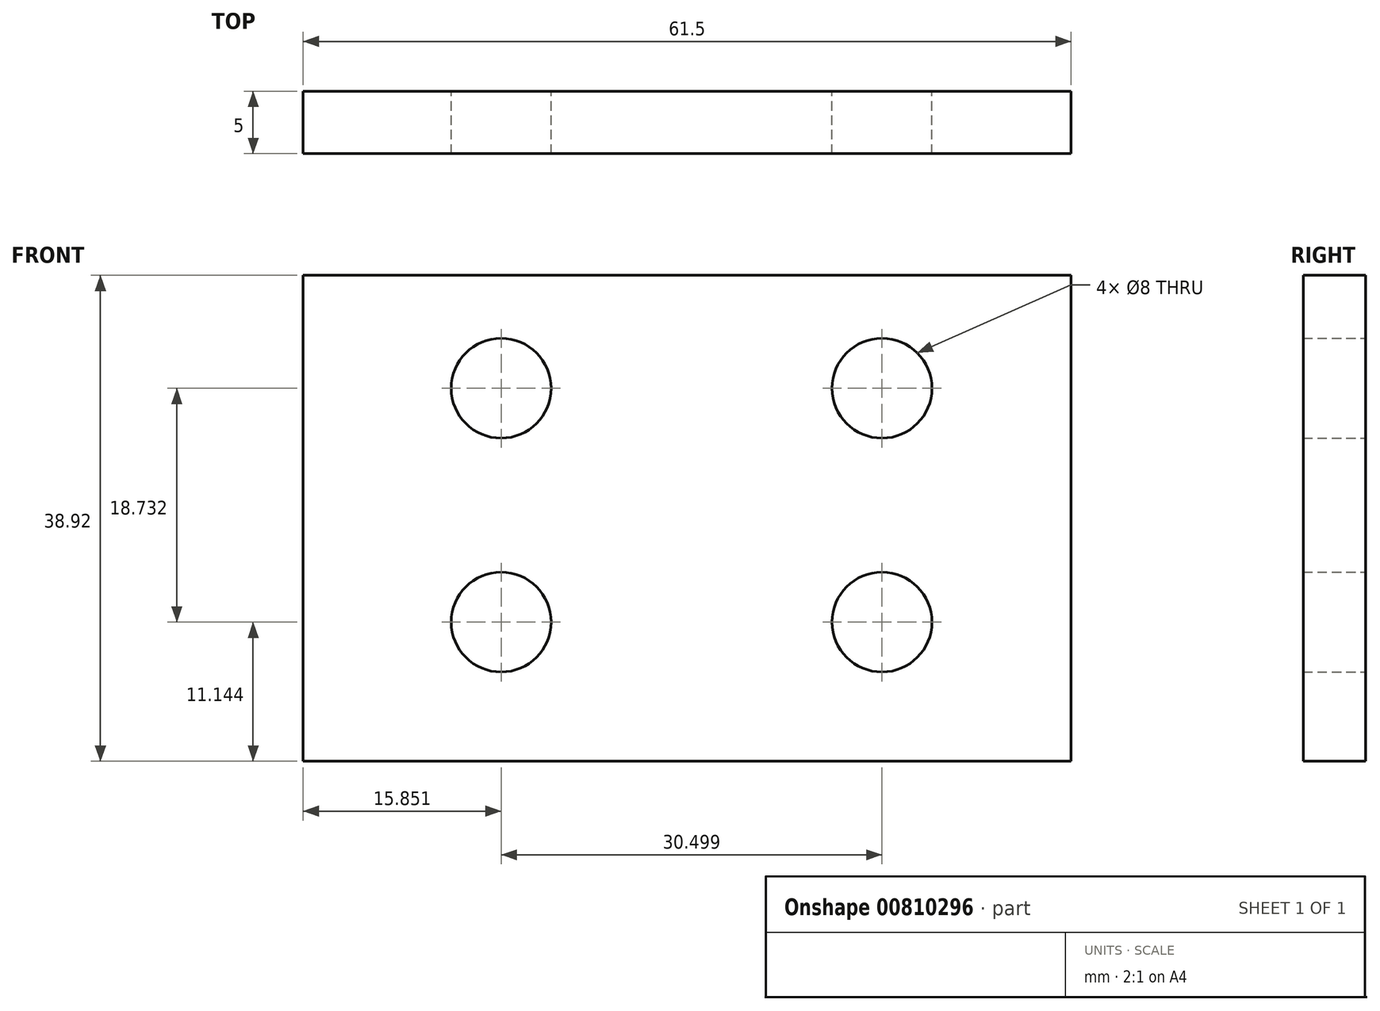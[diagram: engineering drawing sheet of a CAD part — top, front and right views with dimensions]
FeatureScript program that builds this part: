
annotation { "Feature Type Name" : "Feature", "Feature Type Description" : "" }
export const myFeature = defineFeature(function(context is Context, id is Id, definition is map)
    precondition{}
    {
        {
            var Q0;
            Q0=qCreatedBy(makeId("Front.planeOp"),FACE);
            var sketch = newSketch(context, id + "F0", { "sketchPlane" : qUnion([Q0])});
            skLineSegment(sketch, "E0.bottom", {"start": v(-31.1, 18.41) * mm, "end": v(30.4, 18.41) * mm});
            skLineSegment(sketch, "E0.top", {"start": v(-31.1, -20.5) * mm, "end": v(30.4, -20.5) * mm});
            skLineSegment(sketch, "E0.left", {"start": v(-31.1, 18.41) * mm, "end": v(-31.1, -20.5) * mm});
            skLineSegment(sketch, "E0.right", {"start": v(30.4, 18.41) * mm, "end": v(30.4, -20.5) * mm});
            skCircle(sketch, "E1", {"center": v(-15.25, 9.37) * mm, "radius": 4 * mm});
            skCircle(sketch, "E2.MirrorC", {"center": v(15.25, 9.37) * mm, "radius": 4 * mm});
            skCircle(sketch, "E3.MirrorC", {"center": v(-15.25, -9.37) * mm, "radius": 4 * mm});
            skCircle(sketch, "E4.MirrorC", {"center": v(15.25, -9.37) * mm, "radius": 4 * mm});
            skSolve(sketch);
        }
        {
            var Q0;
            Q0 = qSketchRegion(id + "F0", true);
            var Q1;
            Q1=makeQuery(id+"F0.imprint","IMPRINT",FACE,{"disambiguationData":[TD([[makeQuery(id+"F0.imprint","IMPRINT",EDGE,{"derivedFrom":sQuery(id+"F0.wireOp",EDGE,"E0.bottom")}),-1.0]])]});
            extrude(context, id + "F1", {"entities" : qUnion([Q0, Q1]), "depth" : 5 * mm, "offsetDistance" : 25.4 * mm});
        }
    });
